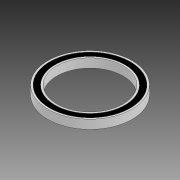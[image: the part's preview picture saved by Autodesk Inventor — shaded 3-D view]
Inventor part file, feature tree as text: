
AUTODESK INVENTOR PART (.ipt)
format: ipt  version: 2020 (Build 240168000, 168)  size: 126,976 bytes
history: native  units: mm
features: revolve x1, sketch x1
ambient origin geometry x8: Origin, YZ Plane, XZ Plane, XY Plane, X Axis, Y Axis, Z Axis, Center Point
bodies: Solid1 (feature_tree)
feature tree (2):
  revolve  "Revolution1"  [1 undecoded]
  sketch  "Sketch1"  dims[d0=37.5mm d2=10.0mm d5=47.5mm d6=0.2mm d7=2.0mm d8=90.0deg]
note: 1 required parameter value undecoded (feature->parameter linkage not recoverable at this tier; creation-order binding heuristic only, values carry confidence <= 0.55)
